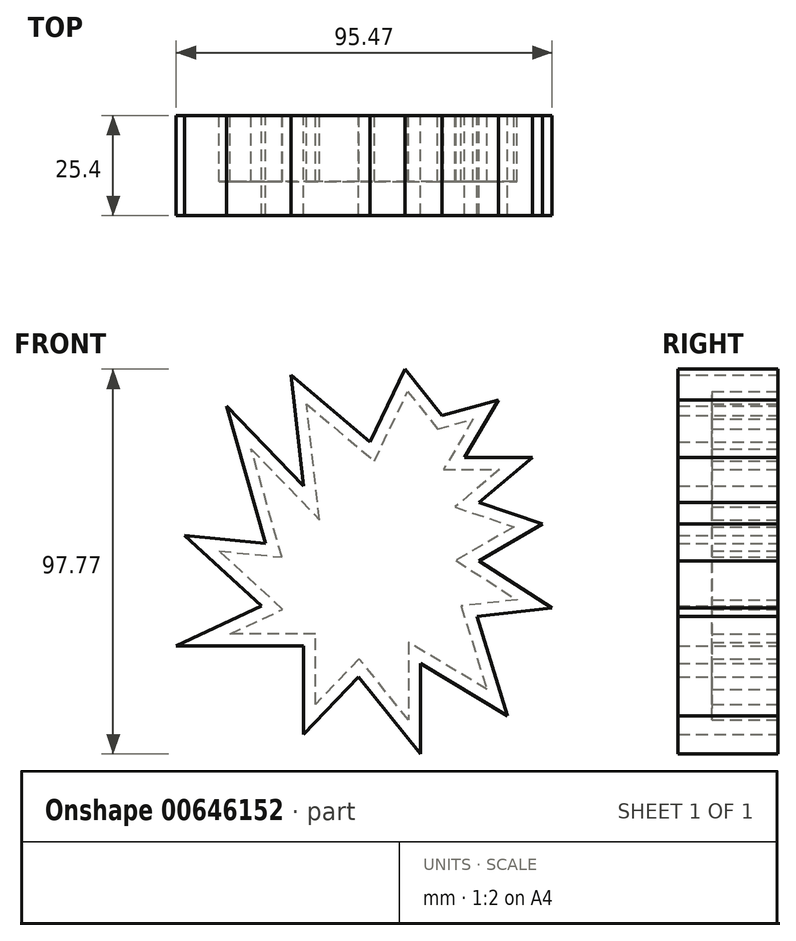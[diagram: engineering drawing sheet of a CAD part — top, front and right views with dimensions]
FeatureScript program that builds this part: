
annotation { "Feature Type Name" : "Feature", "Feature Type Description" : "" }
export const myFeature = defineFeature(function(context is Context, id is Id, definition is map)
    precondition{}
    {
        {
            var Q0;
            Q0=qCreatedBy(makeId("Front.planeOp"),FACE);
            var sketch = newSketch(context, id + "F0", { "sketchPlane" : qUnion([Q0])});
            skLineSegment(sketch, "E0", {"start": v(11.88, 42.32) * mm, "end": v(3.01, 23.81) * mm});
            skLineSegment(sketch, "E1", {"start": v(3.01, 23.81) * mm, "end": v(-17.06, 40.76) * mm});
            skLineSegment(sketch, "E2", {"start": v(-17.06, 40.76) * mm, "end": v(-13.93, 12.6) * mm});
            skLineSegment(sketch, "E3", {"start": v(-13.93, 12.6) * mm, "end": v(-33.49, 32.94) * mm});
            skLineSegment(sketch, "E4", {"start": v(-33.49, 32.94) * mm, "end": v(-23.58, -2) * mm});
            skLineSegment(sketch, "E5", {"start": v(-23.58, -2) * mm, "end": v(-44.18, 0) * mm});
            skLineSegment(sketch, "E6", {"start": v(-44.18, 0) * mm, "end": v(-24.62, -17.9) * mm});
            skLineSegment(sketch, "E7", {"start": v(-24.62, -17.9) * mm, "end": v(-46.26, -28.07) * mm});
            skLineSegment(sketch, "E8", {"start": v(-46.26, -28.07) * mm, "end": v(-13.93, -28.07) * mm});
            skLineSegment(sketch, "E9", {"start": v(-13.93, -28.07) * mm, "end": v(-13.93, -50.5) * mm});
            skLineSegment(sketch, "E10", {"start": v(-13.93, -50.5) * mm, "end": v(0, -35.9) * mm});
            skLineSegment(sketch, "E11", {"start": v(0, -35.9) * mm, "end": v(15.79, -55.45) * mm});
            skLineSegment(sketch, "E12", {"start": v(15.79, -55.45) * mm, "end": v(15.79, -32.5) * mm});
            skLineSegment(sketch, "E13", {"start": v(15.79, -32.5) * mm, "end": v(37.95, -45.8) * mm});
            skLineSegment(sketch, "E14", {"start": v(37.95, -45.8) * mm, "end": v(30.13, -20.51) * mm});
            skLineSegment(sketch, "E15", {"start": v(30.13, -20.51) * mm, "end": v(49.21, -18.4) * mm});
            skLineSegment(sketch, "E16", {"start": v(49.21, -18.4) * mm, "end": v(30.65, -6.43) * mm});
            skLineSegment(sketch, "E17", {"start": v(30.65, -6.43) * mm, "end": v(46.81, 2.95) * mm});
            skLineSegment(sketch, "E18", {"start": v(46.81, 2.95) * mm, "end": v(30.65, 8.43) * mm});
            skLineSegment(sketch, "E19", {"start": v(30.65, 8.43) * mm, "end": v(44.2, 19.9) * mm});
            skLineSegment(sketch, "E20", {"start": v(44.2, 19.9) * mm, "end": v(27, 19.9) * mm});
            skLineSegment(sketch, "E21", {"start": v(27, 19.9) * mm, "end": v(35.6, 34.5) * mm});
            skLineSegment(sketch, "E22", {"start": v(35.6, 34.5) * mm, "end": v(21.26, 30.59) * mm});
            skLineSegment(sketch, "E23", {"start": v(21.26, 30.59) * mm, "end": v(11.88, 42.32) * mm});
            skSolve(sketch);
        }
        {
            var Q0;
            Q0=makeQuery(id+"F0.imprint","IMPRINT",FACE,{"disambiguationData":[TD([[makeQuery(id+"F0.imprint","IMPRINT",EDGE,{"derivedFrom":sQuery(id+"F0.wireOp",EDGE,"E0")}),1.0]])]});
            extrude(context, id + "F1", {"entities" : qUnion([Q0]), "depth" : 25.4 * mm, "offsetDistance" : 25.4 * mm});
        }
        {
            var Q0;
            Q0=makeQuery(id+"F1.opExtrude","CAP_FACE",FACE,{"disambiguationData":[OSD([sQuery(id+"F0.wireOp",EDGE,"E0"),sQuery(id+"F0.wireOp",EDGE,"E1"),sQuery(id+"F0.wireOp",EDGE,"E2"),sQuery(id+"F0.wireOp",EDGE,"E3"),sQuery(id+"F0.wireOp",EDGE,"E4"),sQuery(id+"F0.wireOp",EDGE,"E5"),sQuery(id+"F0.wireOp",EDGE,"E6"),sQuery(id+"F0.wireOp",EDGE,"E7"),sQuery(id+"F0.wireOp",EDGE,"E8"),sQuery(id+"F0.wireOp",EDGE,"E9"),sQuery(id+"F0.wireOp",EDGE,"E10"),sQuery(id+"F0.wireOp",EDGE,"E11"),sQuery(id+"F0.wireOp",EDGE,"E12"),sQuery(id+"F0.wireOp",EDGE,"E13"),sQuery(id+"F0.wireOp",EDGE,"E14"),sQuery(id+"F0.wireOp",EDGE,"E15"),sQuery(id+"F0.wireOp",EDGE,"E16"),sQuery(id+"F0.wireOp",EDGE,"E17"),sQuery(id+"F0.wireOp",EDGE,"E18"),sQuery(id+"F0.wireOp",EDGE,"E19"),sQuery(id+"F0.wireOp",EDGE,"E20"),sQuery(id+"F0.wireOp",EDGE,"E21"),sQuery(id+"F0.wireOp",EDGE,"E22"),sQuery(id+"F0.wireOp",EDGE,"E23")])],"isStart":true});
            var sketch = newSketch(context, id + "F2", { "sketchPlane" : qUnion([Q0])});
            skLineSegment(sketch, "E24.0", {"start": v(-12.53, 36.63) * mm, "end": v(-20.13, 27.12) * mm});
            skLineSegment(sketch, "E24.1", {"start": v(-12.74, -27.12) * mm, "end": v(-12.74, -46.82) * mm});
            skLineSegment(sketch, "E24.2", {"start": v(-32.68, -39.09) * mm, "end": v(-12.74, -27.12) * mm});
            skLineSegment(sketch, "E24.3", {"start": v(-26.13, -17.89) * mm, "end": v(-32.68, -39.09) * mm});
            skLineSegment(sketch, "E24.4", {"start": v(-40.35, -16.3) * mm, "end": v(-26.13, -17.89) * mm});
            skLineSegment(sketch, "E24.5", {"start": v(-24.81, -6.3) * mm, "end": v(-40.35, -16.3) * mm});
            skLineSegment(sketch, "E24.6", {"start": v(-39.48, 2.22) * mm, "end": v(-24.81, -6.3) * mm});
            skLineSegment(sketch, "E24.7", {"start": v(-29.17, 29.59) * mm, "end": v(-21.67, 16.85) * mm});
            skLineSegment(sketch, "E24.8", {"start": v(-21.67, 16.85) * mm, "end": v(-35.89, 16.85) * mm});
            skLineSegment(sketch, "E24.9", {"start": v(-35.89, 16.85) * mm, "end": v(-24.56, 7.27) * mm});
            skLineSegment(sketch, "E24.10", {"start": v(-24.56, 7.27) * mm, "end": v(-39.48, 2.22) * mm});
            skLineSegment(sketch, "E24.11", {"start": v(-12.74, -46.82) * mm, "end": v(-0.2, -31.28) * mm});
            skLineSegment(sketch, "E24.12", {"start": v(-20.13, 27.12) * mm, "end": v(-29.17, 29.59) * mm});
            skLineSegment(sketch, "E24.13", {"start": v(-0.2, -31.28) * mm, "end": v(10.89, -42.88) * mm});
            skLineSegment(sketch, "E24.14", {"start": v(10.89, -42.88) * mm, "end": v(10.89, -25.02) * mm});
            skLineSegment(sketch, "E24.15", {"start": v(10.89, -25.02) * mm, "end": v(32.6, -25.02) * mm});
            skLineSegment(sketch, "E24.16", {"start": v(32.6, -25.02) * mm, "end": v(19.2, -18.73) * mm});
            skLineSegment(sketch, "E24.17", {"start": v(19.2, -18.73) * mm, "end": v(35.39, -3.92) * mm});
            skLineSegment(sketch, "E24.18", {"start": v(35.39, -3.92) * mm, "end": v(19.43, -5.47) * mm});
            skLineSegment(sketch, "E24.19", {"start": v(19.43, -5.47) * mm, "end": v(27.22, 22.03) * mm});
            skLineSegment(sketch, "E24.20", {"start": v(27.22, 22.03) * mm, "end": v(9.91, 4.02) * mm});
            skLineSegment(sketch, "E24.21", {"start": v(9.91, 4.02) * mm, "end": v(13.19, 33.5) * mm});
            skLineSegment(sketch, "E24.22", {"start": v(13.19, 33.5) * mm, "end": v(-4.06, 18.94) * mm});
            skLineSegment(sketch, "E24.23", {"start": v(-4.06, 18.94) * mm, "end": v(-12.53, 36.63) * mm});
            skSolve(sketch);
        }
        {
            var Q0;
            Q0=makeQuery(id+"F2.imprint","IMPRINT",FACE,{"disambiguationData":[TD([[makeQuery(id+"F2.imprint","IMPRINT",EDGE,{"derivedFrom":sQuery(id+"F2.wireOp",EDGE,"E24.0")}),1.0]])]});
            extrude(context, id + "F3", {"entities" : qUnion([Q0]), "operationType" : NewBodyOperationType.REMOVE, "oppositeDirection" : true, "depth" : 16.76 * mm, "offsetDistance" : 25.4 * mm});
        }
    });
